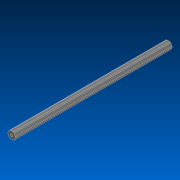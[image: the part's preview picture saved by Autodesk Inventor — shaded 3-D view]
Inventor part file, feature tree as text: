
AUTODESK INVENTOR PART (.ipt)
format: ipt  version: 2022.2 (Build 262287000, 287)  size: 121,344 bytes
history: native  units: in
note: dims shown in document units (in); Inventor stores cm internally (conversion verified against a paired STEP export)
features: extrude x1, sketch x1, other x1
ambient origin geometry x8: Origin, YZ Plane, XZ Plane, XY Plane, X Axis, Y Axis, Z Axis, Center Point
bodies: Solid1 (feature_tree)
feature tree (3):
  extrude  "Extrusion1"  TaperAngle=0.0deg  [1 undecoded]
  sketch  "Sketch1"  dims[d0=25.0in d1=0.0in]
  other  "Cut-Extrude2"
note: 1 required parameter value undecoded (feature->parameter linkage not recoverable at this tier; creation-order binding heuristic only, values carry confidence <= 0.55)
